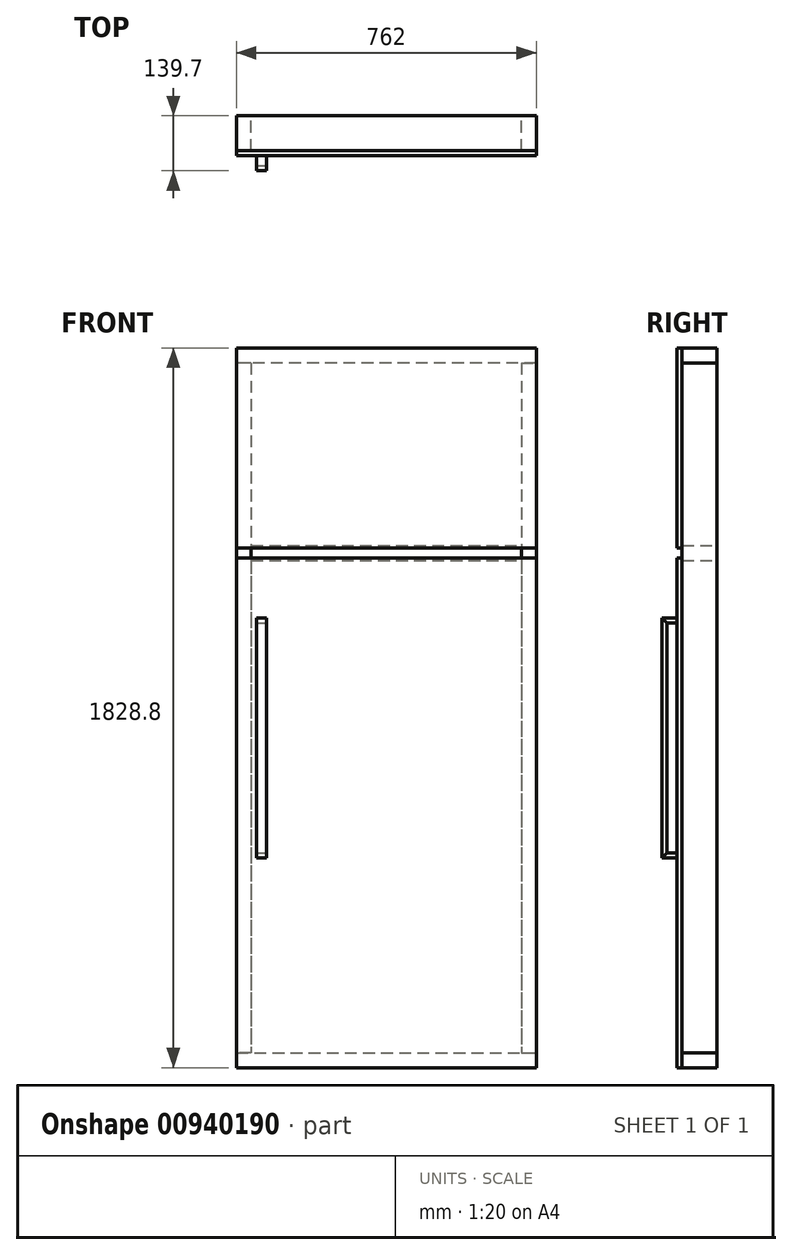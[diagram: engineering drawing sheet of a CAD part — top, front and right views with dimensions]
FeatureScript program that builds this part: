
annotation { "Feature Type Name" : "Feature", "Feature Type Description" : "" }
export const myFeature = defineFeature(function(context is Context, id is Id, definition is map)
    precondition{}
    {
        {
            var Q0;
            Q0=qCreatedBy(makeId("Front.planeOp"),FACE);
            var sketch = newSketch(context, id + "F0", { "sketchPlane" : qUnion([Q0])});
            skLineSegment(sketch, "E0.bottom", {"start": v(342.9, -876.3) * mm, "end": v(-342.9, -876.3) * mm, "construction": true});
            skLineSegment(sketch, "E0.top", {"start": v(342.9, 876.3) * mm, "end": v(-342.9, 876.3) * mm, "construction": true});
            skLineSegment(sketch, "E0.left", {"start": v(342.9, -876.3) * mm, "end": v(342.9, 876.3) * mm, "construction": true});
            skLineSegment(sketch, "E0.right", {"start": v(-342.9, -876.3) * mm, "end": v(-342.9, 876.3) * mm, "construction": true});
            skPoint(sketch, "E0.middle", {"position": v(0, 0) * mm});
            skLineSegment(sketch, "E1.bottom", {"start": v(342.9, 876.3) * mm, "end": v(381, 876.3) * mm});
            skLineSegment(sketch, "E1.top", {"start": v(342.9, -876.3) * mm, "end": v(381, -876.3) * mm});
            skLineSegment(sketch, "E1.left", {"start": v(342.9, 876.3) * mm, "end": v(342.9, -876.3) * mm});
            skLineSegment(sketch, "E1.right", {"start": v(381, 876.3) * mm, "end": v(381, -876.3) * mm});
            skLineSegment(sketch, "E2.bottom", {"start": v(-342.9, 876.3) * mm, "end": v(-381, 876.3) * mm});
            skLineSegment(sketch, "E2.top", {"start": v(-342.9, -876.3) * mm, "end": v(-381, -876.3) * mm});
            skLineSegment(sketch, "E2.left", {"start": v(-342.9, 876.3) * mm, "end": v(-342.9, -876.3) * mm});
            skLineSegment(sketch, "E2.right", {"start": v(-381, 876.3) * mm, "end": v(-381, -876.3) * mm});
            skLineSegment(sketch, "E3.bottom", {"start": v(-381, -876.3) * mm, "end": v(381, -876.3) * mm});
            skLineSegment(sketch, "E3.top", {"start": v(-381, -914.4) * mm, "end": v(381, -914.4) * mm});
            skLineSegment(sketch, "E3.left", {"start": v(-381, -876.3) * mm, "end": v(-381, -914.4) * mm});
            skLineSegment(sketch, "E3.right", {"start": v(381, -876.3) * mm, "end": v(381, -914.4) * mm});
            skLineSegment(sketch, "E4.bottom", {"start": v(-381, 876.3) * mm, "end": v(381, 876.3) * mm});
            skLineSegment(sketch, "E4.top", {"start": v(-381, 914.4) * mm, "end": v(381, 914.4) * mm});
            skLineSegment(sketch, "E4.left", {"start": v(-381, 876.3) * mm, "end": v(-381, 914.4) * mm});
            skLineSegment(sketch, "E4.right", {"start": v(381, 876.3) * mm, "end": v(381, 914.4) * mm});
            skLineSegment(sketch, "E5.bottom", {"start": v(-342.9, 412.75) * mm, "end": v(342.9, 412.75) * mm});
            skLineSegment(sketch, "E5.top", {"start": v(-342.9, 374.65) * mm, "end": v(342.9, 374.65) * mm});
            skLineSegment(sketch, "E5.left", {"start": v(-342.9, 412.75) * mm, "end": v(-342.9, 374.65) * mm});
            skLineSegment(sketch, "E5.right", {"start": v(342.9, 412.75) * mm, "end": v(342.9, 374.65) * mm});
            skSolve(sketch);
        }
        {
            var Q0;
            Q0=makeQuery(id+"F0.imprint","IMPRINT",FACE,{"disambiguationData":[TD([[makeQuery(id+"F0.imprint","IMPRINT",EDGE,{"derivedFrom":sQuery(id+"F0.wireOp",EDGE,"E4.top")}),-1.0]])]});
            var Q1;
            Q1=makeQuery(id+"F0.imprint","IMPRINT",FACE,{"disambiguationData":[TD([[makeQuery(id+"F0.imprint","IMPRINT",EDGE,{"derivedFrom":sQuery(id+"F0.wireOp",EDGE,"E5.bottom")}),-1.0]])]});
            var Q2;
            Q2=makeQuery(id+"F0.imprint","IMPRINT",FACE,{"disambiguationData":[TD([[makeQuery(id+"F0.imprint","IMPRINT",EDGE,{"derivedFrom":sQuery(id+"F0.wireOp",EDGE,"E3.top")}),1.0]])]});
            extrude(context, id + "F1", {"entities" : qUnion([Q0, Q1, Q2]), "endBound" : BoundingType.SYMMETRIC, "depth" : 88.9 * mm, "offsetDistance" : 25.4 * mm});
        }
        {
            var Q0;
            {var subQ3=sQuery(id+"F0.wireOp",EDGE,"E2.right");Q0=makeQuery(id+"F0.imprint","IMPRINT",FACE,{"disambiguationData":[TD([[makeQuery(id+"F0.imprint","IMPRINT",EDGE,{"derivedFrom":subQ3}),1.0]])]});}
            var Q1;
            {var subQ3=sQuery(id+"F0.wireOp",EDGE,"E1.right");Q1=makeQuery(id+"F0.imprint","IMPRINT",FACE,{"disambiguationData":[TD([[makeQuery(id+"F0.imprint","IMPRINT",EDGE,{"derivedFrom":subQ3}),-1.0]])]});}
            extrude(context, id + "F2", {"entities" : qUnion([Q0, Q1]), "endBound" : BoundingType.SYMMETRIC, "depth" : 88.9 * mm, "offsetDistance" : 25.4 * mm});
        }
        {
            var Q0;
            Q0=makeQuery(id+"F1.opExtrude","CAP_FACE",FACE,{"disambiguationData":[OSD([sQuery(id+"F0.wireOp",EDGE,"E4.bottom"),sQuery(id+"F0.wireOp",EDGE,"E4.top"),sQuery(id+"F0.wireOp",EDGE,"E4.left"),sQuery(id+"F0.wireOp",EDGE,"E4.right")])],"isStart":false});
            var sketch = newSketch(context, id + "F3", { "sketchPlane" : qUnion([Q0])});
            skLineSegment(sketch, "E6.bottom", {"start": v(-381, 914.4) * mm, "end": v(381, 914.4) * mm});
            skLineSegment(sketch, "E6.top", {"start": v(-381, 406.4) * mm, "end": v(381, 406.4) * mm});
            skLineSegment(sketch, "E6.left", {"start": v(-381, 914.4) * mm, "end": v(-381, 406.4) * mm});
            skLineSegment(sketch, "E6.right", {"start": v(381, 914.4) * mm, "end": v(381, 406.4) * mm});
            skSolve(sketch);
        }
        {
            var Q0;
            Q0 = qSketchRegion(id + "F3", true);
            extrude(context, id + "F4", {"entities" : qUnion([Q0]), "depth" : 12.7 * mm, "offsetDistance" : 25.4 * mm});
        }
        {
            var Q0;
            Q0=makeQuery(id+"F1.opExtrude","CAP_FACE",FACE,{"disambiguationData":[OSD([sQuery(id+"F0.wireOp",EDGE,"E3.bottom"),sQuery(id+"F0.wireOp",EDGE,"E3.top"),sQuery(id+"F0.wireOp",EDGE,"E3.left"),sQuery(id+"F0.wireOp",EDGE,"E3.right")])],"isStart":false});
            var sketch = newSketch(context, id + "F5", { "sketchPlane" : qUnion([Q0])});
            skLineSegment(sketch, "E7.bottom", {"start": v(-381, -914.4) * mm, "end": v(381, -914.4) * mm});
            skLineSegment(sketch, "E7.top", {"start": v(-381, 381) * mm, "end": v(381, 381) * mm});
            skLineSegment(sketch, "E7.left", {"start": v(-381, -914.4) * mm, "end": v(-381, 381) * mm});
            skLineSegment(sketch, "E7.right", {"start": v(381, -914.4) * mm, "end": v(381, 381) * mm});
            skSolve(sketch);
        }
        {
            var Q0;
            Q0 = qSketchRegion(id + "F5", true);
            extrude(context, id + "F6", {"entities" : qUnion([Q0]), "depth" : 12.7 * mm, "offsetDistance" : 25.4 * mm});
        }
        {
            var Q0;
            Q0=makeQuery(id+"F2.opExtrude","SWEPT_FACE",FACE,{"disambiguationData":[OSD([sQuery(id+"F0.wireOp",EDGE,"E2.right")])]});
            cPlane(context, id + "F7", {"entities" : qUnion([Q0]), "cplaneType" : CPlaneType.OFFSET, "offset" : 63.5 * mm, "oppositeDirection" : true, "width" : 152.4 * mm, "height" : 152.4 * mm});
        }
        {
            var Q0;
            Q0=qCreatedBy(id+"F7.planeOp",FACE);
            var sketch = newSketch(context, id + "F8", { "sketchPlane" : qUnion([Q0])});
            skLineSegment(sketch, "E8.bottom", {"start": v(57.15, 215.9) * mm, "end": v(82.55, 215.9) * mm, "construction": true});
            skLineSegment(sketch, "E8.top", {"start": v(57.15, -368.3) * mm, "end": v(82.55, -368.3) * mm, "construction": true});
            skLineSegment(sketch, "E8.left", {"start": v(57.15, 215.9) * mm, "end": v(57.15, -368.3) * mm, "construction": true});
            skLineSegment(sketch, "E8.right", {"start": v(82.55, 215.9) * mm, "end": v(82.55, -368.3) * mm, "construction": true});
            skLineSegment(sketch, "E9.bottom", {"start": v(57.15, 215.9) * mm, "end": v(82.55, 215.9) * mm});
            skLineSegment(sketch, "E9.top", {"start": v(57.15, 228.6) * mm, "end": v(82.55, 228.6) * mm});
            skLineSegment(sketch, "E9.left", {"start": v(57.15, 215.9) * mm, "end": v(57.15, 228.6) * mm});
            skLineSegment(sketch, "E9.right", {"start": v(82.55, 215.9) * mm, "end": v(82.55, 228.6) * mm});
            skLineSegment(sketch, "E10.bottom", {"start": v(57.15, -368.3) * mm, "end": v(82.55, -368.3) * mm});
            skLineSegment(sketch, "E10.top", {"start": v(57.15, -381) * mm, "end": v(82.55, -381) * mm});
            skLineSegment(sketch, "E10.left", {"start": v(57.15, -368.3) * mm, "end": v(57.15, -381) * mm});
            skLineSegment(sketch, "E10.right", {"start": v(82.55, -368.3) * mm, "end": v(82.55, -381) * mm});
            skLineSegment(sketch, "E11.bottom", {"start": v(82.55, 228.6) * mm, "end": v(95.25, 228.6) * mm});
            skLineSegment(sketch, "E11.top", {"start": v(82.55, -381) * mm, "end": v(95.25, -381) * mm});
            skLineSegment(sketch, "E11.left", {"start": v(82.55, 228.6) * mm, "end": v(82.55, -381) * mm});
            skLineSegment(sketch, "E11.right", {"start": v(95.25, 228.6) * mm, "end": v(95.25, -381) * mm});
            skLineSegment(sketch, "E12", {"start": v(82.55, 215.9) * mm, "end": v(95.25, 228.6) * mm});
            skLineSegment(sketch, "E13", {"start": v(82.55, -368.3) * mm, "end": v(95.25, -381) * mm});
            skSolve(sketch);
        }
        {
            var Q0;
            {var subQ0=sQuery(id+"F8.wireOp",EDGE,"E9.bottom");Q0=makeQuery(id+"F8.imprint","IMPRINT",FACE,{"disambiguationData":[TD([[makeQuery(id+"F8.imprint","IMPRINT",EDGE,{"derivedFrom":subQ0}),1.0]])]});}
            var Q1;
            {var subQ0=sQuery(id+"F8.wireOp",EDGE,"E11.bottom");Q1=makeQuery(id+"F8.imprint","IMPRINT",FACE,{"disambiguationData":[TD([[makeQuery(id+"F8.imprint","IMPRINT",EDGE,{"derivedFrom":subQ0}),-1.0]])]});}
            var Q2;
            {var subQ0=sQuery(id+"F8.wireOp",EDGE,"E10.bottom");Q2=makeQuery(id+"F8.imprint","IMPRINT",FACE,{"disambiguationData":[TD([[makeQuery(id+"F8.imprint","IMPRINT",EDGE,{"derivedFrom":subQ0}),-1.0]])]});}
            var Q3;
            {var subQ0=sQuery(id+"F8.wireOp",EDGE,"E11.top");Q3=makeQuery(id+"F8.imprint","IMPRINT",FACE,{"disambiguationData":[TD([[makeQuery(id+"F8.imprint","IMPRINT",EDGE,{"derivedFrom":subQ0}),1.0]])]});}
            extrude(context, id + "F9", {"entities" : qUnion([Q0, Q1, Q2, Q3]), "endBound" : BoundingType.SYMMETRIC, "depth" : 25.4 * mm, "offsetDistance" : 25.4 * mm});
        }
        {
            var Q0;
            Q0=makeQuery(id+"F8.imprint","IMPRINT",FACE,{"disambiguationData":[TD([[makeQuery(id+"F8.imprint","IMPRINT",EDGE,{"derivedFrom":sQuery(id+"F8.wireOp",EDGE,"E11.right")}),-1.0]])]});
            extrude(context, id + "F10", {"entities" : qUnion([Q0]), "endBound" : BoundingType.SYMMETRIC, "depth" : 25.4 * mm, "offsetDistance" : 25.4 * mm});
        }
    });
